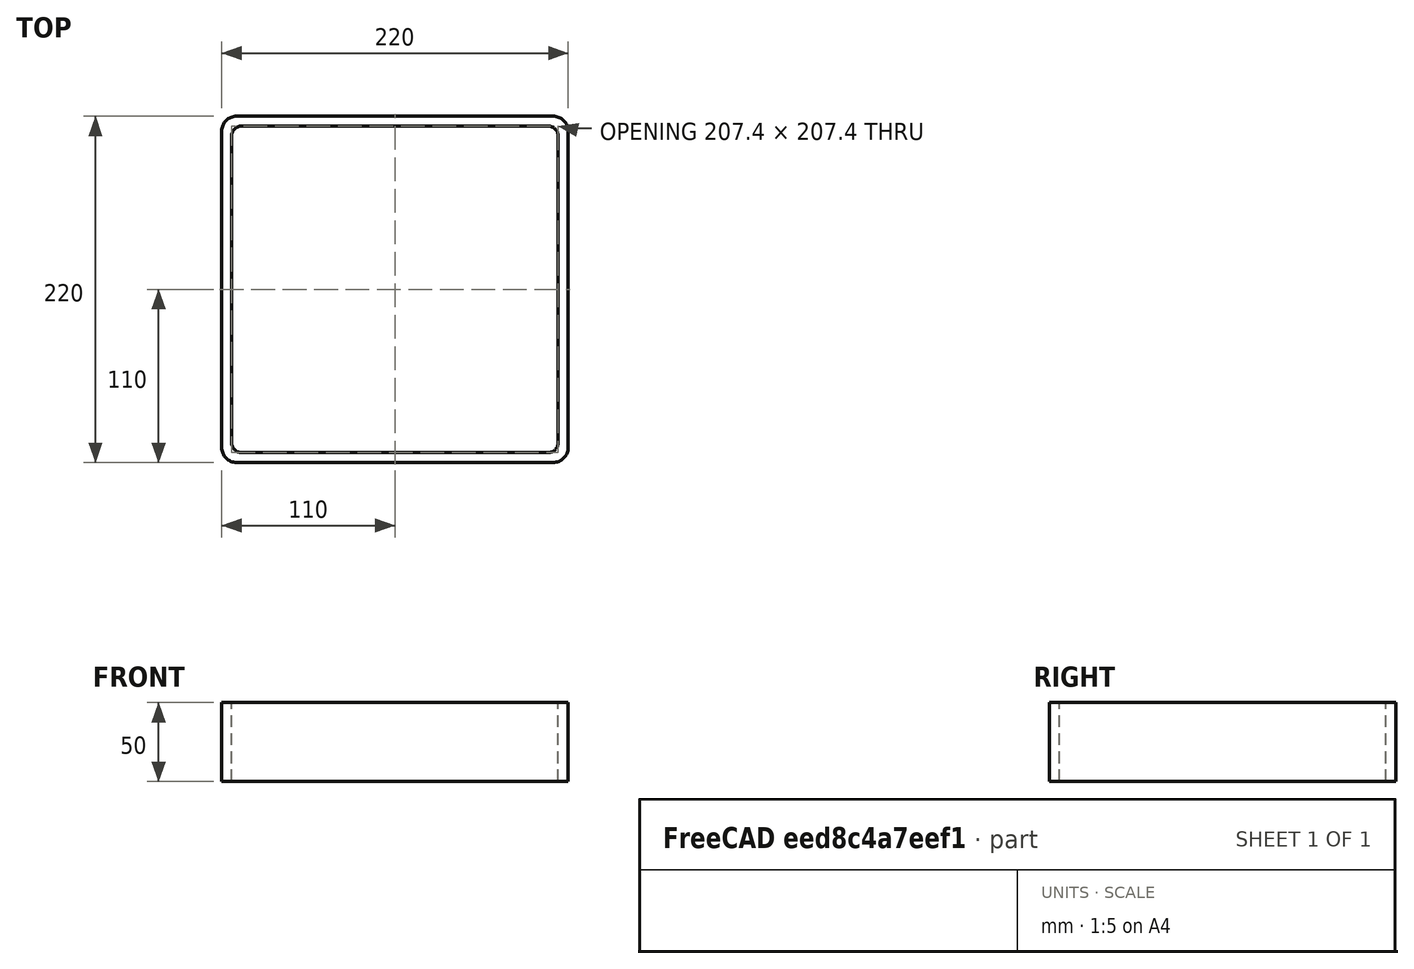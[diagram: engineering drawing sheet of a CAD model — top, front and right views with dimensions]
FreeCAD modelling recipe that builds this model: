
FCSTD DOCUMENT  (FreeCAD 0.15R4671 (Git))
Label: Square hollow section 220x220x6.3 EN10219 S235JRH
License: All rights reserved
LicenseURL: http://en.wikipedia.org/wiki/All_rights_reserved
objects: Sketcher::SketchObject×1, Part::Extrusion×1
note: 2 computed .brp shape members not serialized (recipe doc carries the construction recipe); baked Part::Feature solids carry a one-line shape summary decoded from their .brp

FEATURE [Sketcher::SketchObject] Sketch
  sketch-geometry (16):
    g0: LineSegment StartX=-97.4 StartY=103.7 StartZ=0 EndX=97.4 EndY=103.7 EndZ=0
    g1: LineSegment StartX=103.7 StartY=97.4 StartZ=0 EndX=103.7 EndY=-97.4 EndZ=0
    g2: LineSegment StartX=97.4 StartY=-103.7 StartZ=0 EndX=-97.4 EndY=-103.7 EndZ=0
    g3: LineSegment StartX=-103.7 StartY=-97.4 StartZ=0 EndX=-103.7 EndY=97.4 EndZ=0
    g4: LineSegment StartX=-100.55 StartY=110 StartZ=0 EndX=100.55 EndY=110 EndZ=0
    g5: LineSegment StartX=110 StartY=100.55 StartZ=0 EndX=110 EndY=-100.55 EndZ=0
    g6: LineSegment StartX=100.55 StartY=-110 StartZ=0 EndX=-100.55 EndY=-110 EndZ=0
    g7: LineSegment StartX=-110 StartY=-100.55 StartZ=0 EndX=-110 EndY=100.55 EndZ=0
    g8: ArcOfCircle CenterX=-97.4 CenterY=97.4 CenterZ=0 NormalX=0 NormalY=0 NormalZ=1 Radius=6.3 StartAngle=1.5708 EndAngle=3.14159
    g9: ArcOfCircle CenterX=97.4 CenterY=97.4 CenterZ=0 NormalX=0 NormalY=0 NormalZ=1 Radius=6.3 StartAngle=0 EndAngle=1.5708
    g10: ArcOfCircle CenterX=97.4 CenterY=-97.4 CenterZ=0 NormalX=0 NormalY=0 NormalZ=1 Radius=6.3 StartAngle=4.71239 EndAngle=6.28319
    g11: ArcOfCircle CenterX=-97.4 CenterY=-97.4 CenterZ=0 NormalX=0 NormalY=0 NormalZ=1 Radius=6.3 StartAngle=3.14159 EndAngle=4.71239
    g12: ArcOfCircle CenterX=100.55 CenterY=100.55 CenterZ=0 NormalX=0 NormalY=0 NormalZ=1 Radius=9.45 StartAngle=0 EndAngle=1.5708
    g13: ArcOfCircle CenterX=100.55 CenterY=-100.55 CenterZ=0 NormalX=0 NormalY=0 NormalZ=1 Radius=9.45 StartAngle=4.71239 EndAngle=6.28319
    g14: ArcOfCircle CenterX=-100.55 CenterY=-100.55 CenterZ=0 NormalX=0 NormalY=0 NormalZ=1 Radius=9.45 StartAngle=3.14159 EndAngle=4.71239
    g15: ArcOfCircle CenterX=-100.55 CenterY=100.55 CenterZ=0 NormalX=0 NormalY=0 NormalZ=1 Radius=9.45 StartAngle=1.5708 EndAngle=3.14159
  constraints (36):
    c: Horizontal(g2)
    c: Vertical(g3)
    c: Horizontal(g6)
    c: Vertical(g7)
    c: Tangent(g3,g8) = 1.5708
    c: Tangent(g0,g8) = 1.5708
    c: Tangent(g0,g9) = 1.5708
    c: Tangent(g1,g9) = 1.5708
    c: Tangent(g1,g10) = 1.5708
    c: Tangent(g2,g10) = 1.5708
    c: Tangent(g2,g11) = 1.5708
    c: Tangent(g3,g11) = 1.5708
    c: Tangent(g4,g12) = 1.5708
    c: Tangent(g5,g12) = 1.5708
    c: Tangent(g5,g13) = 1.5708
    c: Tangent(g6,g13) = 1.5708
    c: Tangent(g6,g14) = 1.5708
    c: Tangent(g7,g14) = 1.5708
    c: Tangent(g7,g15) = 1.5708
    c: Tangent(g4,g15) = 1.5708
    c: Equal(g9,g8)
    c: Equal(g9,g11)
    c: Equal(g9,g10)
    c: Equal(g12,g15)
    c: Equal(g12,g14)
    c: Equal(g12,g13)
    c: Symmetric(g4,g6,g-1)
    c: Symmetric(g7,g5,g-2)
    c: DistanceY(g4,g6) = -220
    c: DistanceX(g7,g5) = 220
    c: Symmetric(g3,g1,g-2)
    c: Symmetric(g0,g2,g-1)
    c: DistanceY(g0,g4) = 6.3
    c: DistanceX(g5,g1) = -6.3
    c: Radius(g9) = 6.3
    c: Radius(g12) = 9.45
FEATURE [Part::Extrusion] Extrude  label="Square hollow section 220x220x6.3 EN10219 S235JRH"
  Base = -> Sketch
  Dir = (0,0,50)
  Solid = true
